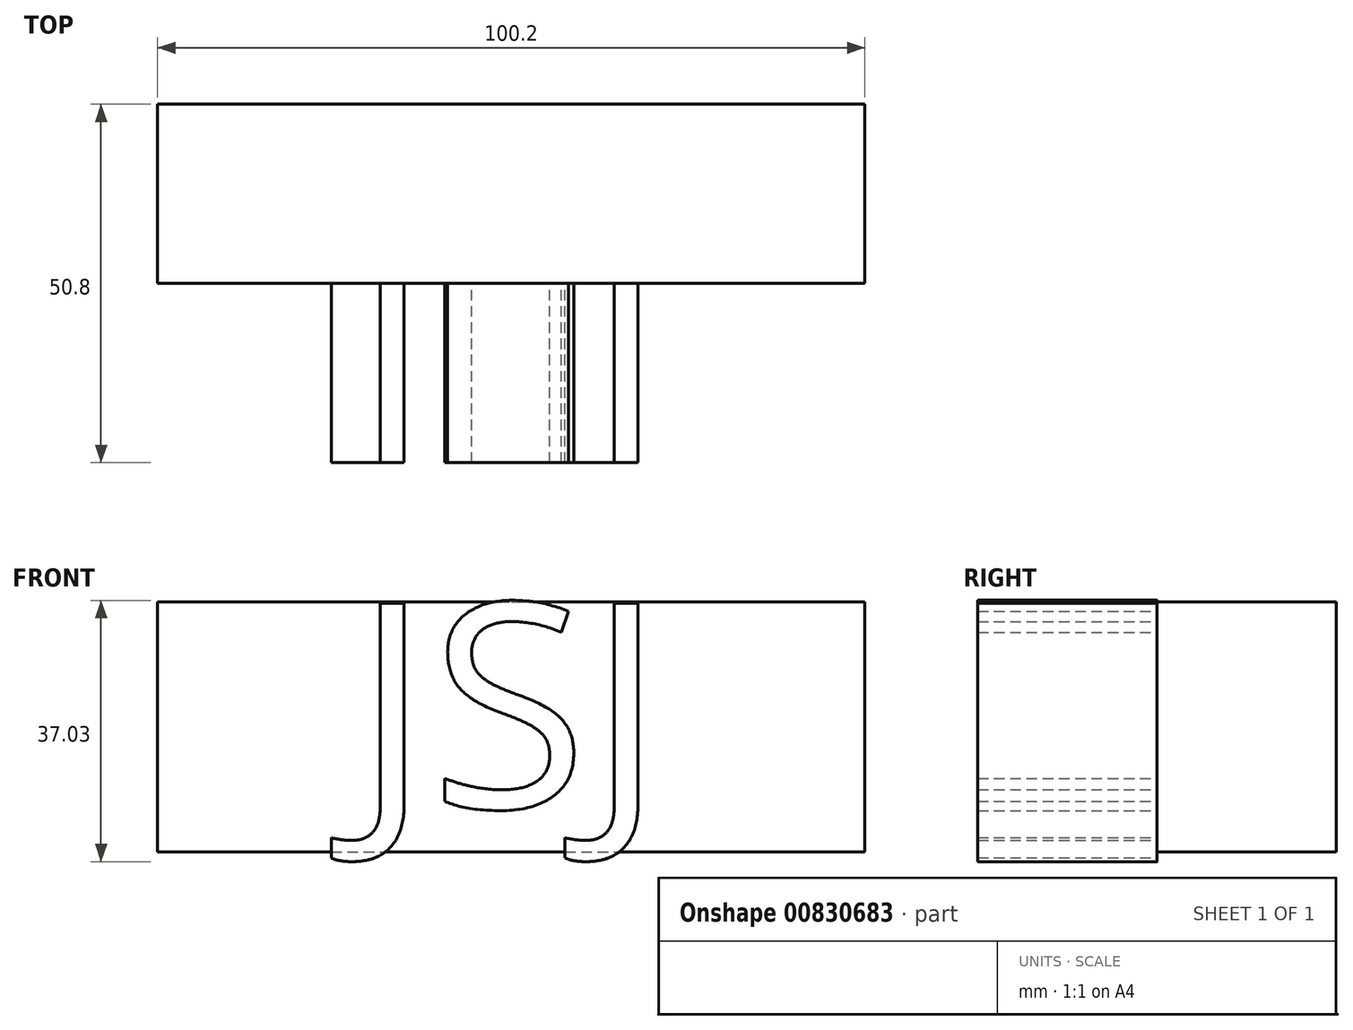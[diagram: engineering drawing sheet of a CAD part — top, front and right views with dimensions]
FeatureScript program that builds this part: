
annotation { "Feature Type Name" : "Feature", "Feature Type Description" : "" }
export const myFeature = defineFeature(function(context is Context, id is Id, definition is map)
    precondition{}
    {
        {
            var Q0;
            Q0=qCreatedBy(makeId("Front.planeOp"),FACE);
            var sketch = newSketch(context, id + "F0", { "sketchPlane" : qUnion([Q0])});
            skLineSegment(sketch, "E0.bottom", {"start": v(0, 0) * mm, "end": v(100.2, 0) * mm});
            skLineSegment(sketch, "E0.top", {"start": v(0, 35.49) * mm, "end": v(100.2, 35.49) * mm});
            skLineSegment(sketch, "E0.left", {"start": v(0, 0) * mm, "end": v(0, 35.49) * mm});
            skLineSegment(sketch, "E0.right", {"start": v(100.2, 0) * mm, "end": v(100.2, 35.49) * mm});
            skSolve(sketch);
        }
        {
            var Q0;
            Q0 = qSketchRegion(id + "F0", true);
            extrude(context, id + "F1", {"entities" : qUnion([Q0]), "depth" : 25.4 * mm, "offsetDistance" : 25.4 * mm});
        }
        {
            var Q0;
            Q0=makeQuery(id+"F1.opExtrude","CAP_FACE",FACE,{"disambiguationData":[OSD([sQuery(id+"F0.wireOp",EDGE,"E0.bottom"),sQuery(id+"F0.wireOp",EDGE,"E0.top"),sQuery(id+"F0.wireOp",EDGE,"E0.left"),sQuery(id+"F0.wireOp",EDGE,"E0.right")])],"isStart":false});
            var sketch = newSketch(context, id + "F2", { "sketchPlane" : qUnion([Q0])});
            skText(sketch, "E1", { "text": "JSJ", "fontName": "OpenSans-Regular.ttf"});
            const initialGuessF2  = {"E1": [0.02777, 0.00628, 1, 0, 0.02924]};
            skSetInitialGuess(sketch, initialGuessF2);
            skSolve(sketch);
        }
        {
            var Q0;
            Q0 = qSketchRegion(id + "F2", true);
            extrude(context, id + "F3", {"entities" : qUnion([Q0]), "operationType" : NewBodyOperationType.ADD, "depth" : 25.4 * mm, "offsetDistance" : 25.4 * mm});
        }
    });
